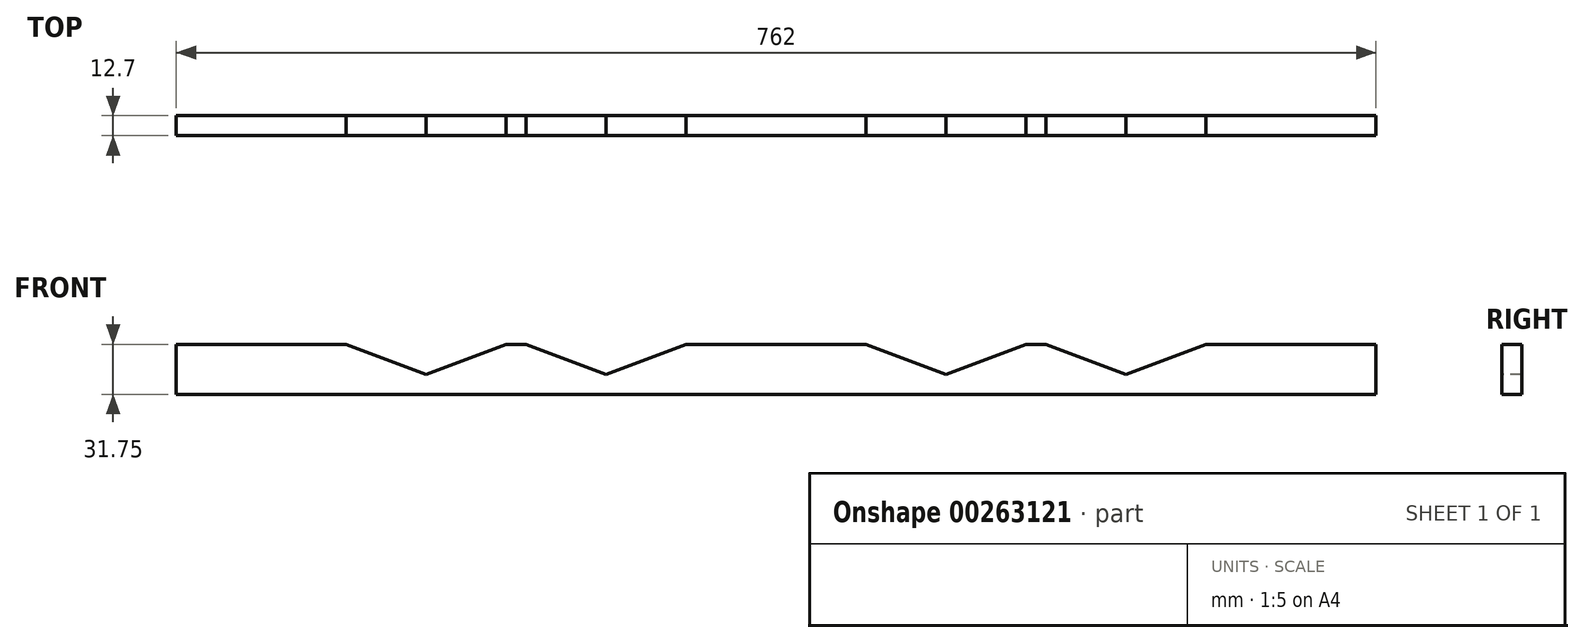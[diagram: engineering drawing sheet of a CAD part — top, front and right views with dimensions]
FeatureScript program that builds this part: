
annotation { "Feature Type Name" : "Feature", "Feature Type Description" : "" }
export const myFeature = defineFeature(function(context is Context, id is Id, definition is map)
    precondition{}
    {
        {
            var Q0;
            Q0=qCreatedBy(makeId("Front.planeOp"),FACE);
            var sketch = newSketch(context, id + "F0", { "sketchPlane" : qUnion([Q0])});
            skLineSegment(sketch, "E0.bottom", {"start": v(-381, 31.75) * mm, "end": v(381, 31.75) * mm});
            skLineSegment(sketch, "E0.top", {"start": v(-381, 0) * mm, "end": v(381, 0) * mm});
            skLineSegment(sketch, "E0.left", {"start": v(-381, 31.75) * mm, "end": v(-381, 0) * mm});
            skLineSegment(sketch, "E0.right", {"start": v(381, 31.75) * mm, "end": v(381, 0) * mm});
            skLineSegment(sketch, "E1.bottom", {"start": v(0, 0) * mm, "end": v(0, 0) * mm});
            skLineSegment(sketch, "E1.top", {"start": v(0, 31.75) * mm, "end": v(0, 31.75) * mm});
            skLineSegment(sketch, "E1.left", {"start": v(0, 0) * mm, "end": v(0, 31.75) * mm});
            skLineSegment(sketch, "E1.right", {"start": v(0, 0) * mm, "end": v(0, 31.75) * mm});
            skSolve(sketch);
        }
        {
            var Q0;
            Q0 = qSketchRegion(id + "F0", true);
            extrude(context, id + "F1", {"entities" : qUnion([Q0]), "oppositeDirection" : true, "depth" : 12.7 * mm});
        }
        {
            var Q0;
            Q0=makeQuery(id+"F1.opExtrude","CAP_FACE",FACE,{"disambiguationData":[OSD([sQuery(id+"F0.wireOp",EDGE,"E0.bottom"),sQuery(id+"F0.wireOp",EDGE,"E0.top"),sQuery(id+"F0.wireOp",EDGE,"E0.left"),sQuery(id+"F0.wireOp",EDGE,"E0.right")])],"isStart":true});
            var sketch = newSketch(context, id + "F2", { "sketchPlane" : qUnion([Q0])});
            skLineSegment(sketch, "E2", {"start": v(-57.15, 31.75) * mm, "end": v(-107.95, 12.7) * mm});
            skLineSegment(sketch, "E3", {"start": v(-107.95, 12.7) * mm, "end": v(-158.75, 31.75) * mm});
            skCircle(sketch, "E4", {"center": v(-107.95, 73.74) * mm, "radius": 57.15 * mm, "construction": true});
            skLineSegment(sketch, "E5", {"start": v(-158.75, 31.75) * mm, "end": v(-57.15, 31.75) * mm});
            skLineSegment(sketch, "E6", {"start": v(-165.1, 0) * mm, "end": v(-165.1, 73.74) * mm, "construction": true});
            skLineSegment(sketch, "E7.MirrorCS", {"start": v(-222.25, 12.7) * mm, "end": v(-171.45, 31.75) * mm});
            skLineSegment(sketch, "E8.MirrorCS", {"start": v(-171.45, 31.75) * mm, "end": v(-273.05, 31.75) * mm});
            skLineSegment(sketch, "E9.MirrorCS", {"start": v(-273.05, 31.75) * mm, "end": v(-222.25, 12.7) * mm});
            skLineSegment(sketch, "E10", {"start": v(-50.8, 0) * mm, "end": v(-50.8, 73.74) * mm, "construction": true});
            skLineSegment(sketch, "E11.MirrorCS", {"start": v(107.95, 12.7) * mm, "end": v(158.75, 31.75) * mm});
            skLineSegment(sketch, "E12.MirrorCS", {"start": v(222.25, 12.7) * mm, "end": v(171.45, 31.75) * mm});
            skLineSegment(sketch, "E13.MirrorCS", {"start": v(158.75, 31.75) * mm, "end": v(57.15, 31.75) * mm});
            skLineSegment(sketch, "E14.MirrorCS", {"start": v(273.05, 31.75) * mm, "end": v(222.25, 12.7) * mm});
            skLineSegment(sketch, "E15.MirrorCS", {"start": v(171.45, 31.75) * mm, "end": v(273.05, 31.75) * mm});
            skLineSegment(sketch, "E16.MirrorCS", {"start": v(57.15, 31.75) * mm, "end": v(107.95, 12.7) * mm});
            skSolve(sketch);
        }
        {
            var Q0;
            Q0 = qSketchRegion(id + "F2", true);
            extrude(context, id + "F3", {"entities" : qUnion([Q0]), "operationType" : NewBodyOperationType.REMOVE, "endBound" : BoundingType.THROUGH_ALL, "oppositeDirection" : true, "depth" : 25.4 * mm});
        }
    });
